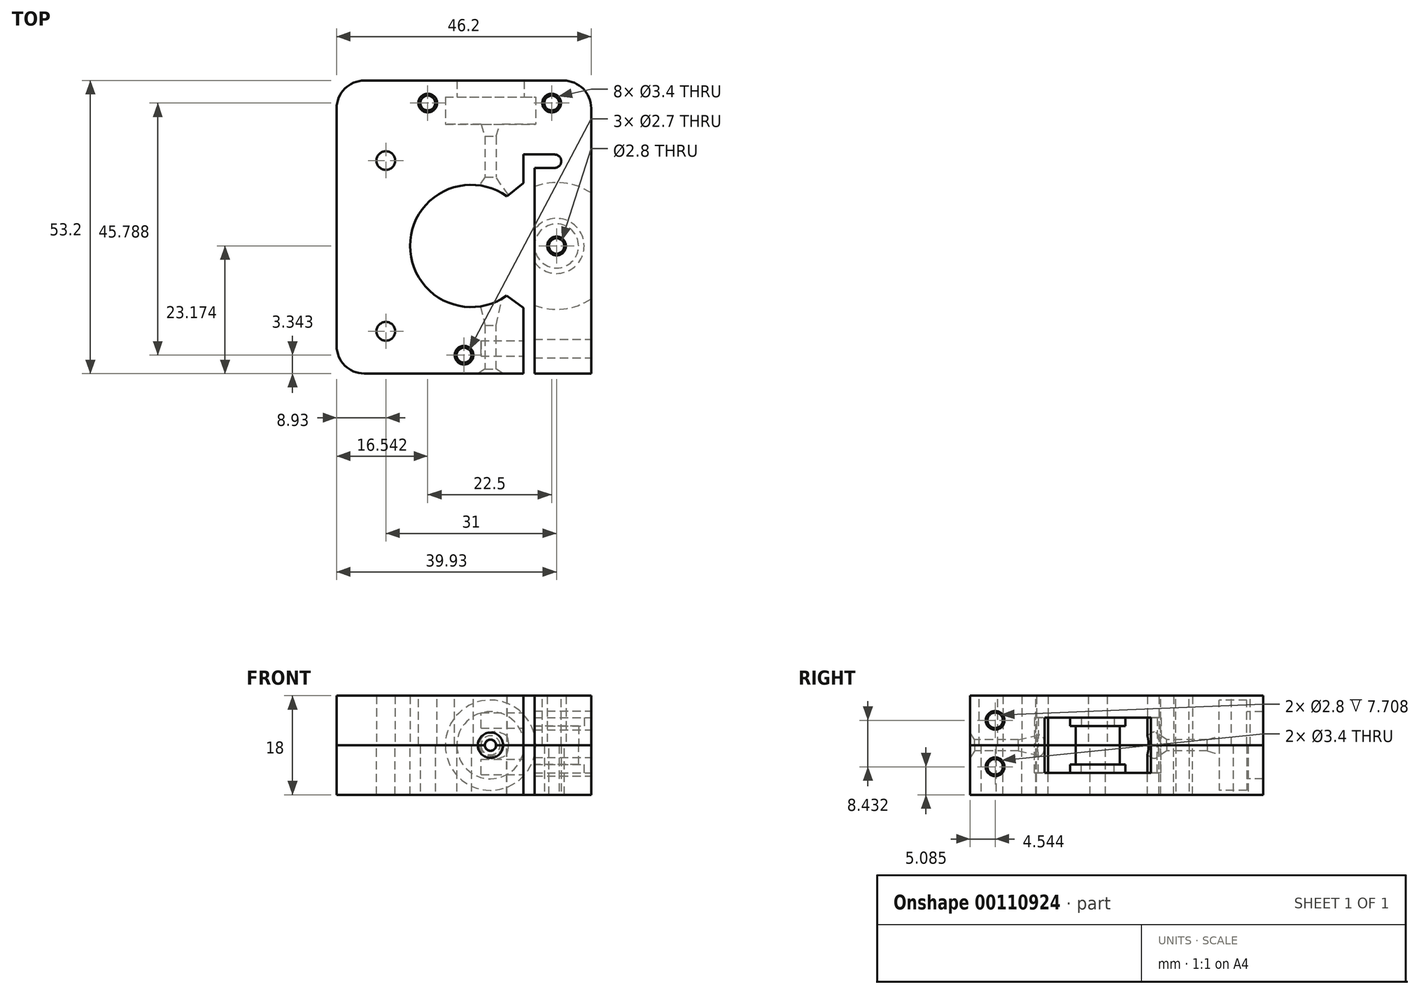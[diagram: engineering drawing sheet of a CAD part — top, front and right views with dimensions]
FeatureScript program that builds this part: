
annotation { "Feature Type Name" : "Feature", "Feature Type Description" : "" }
export const myFeature = defineFeature(function(context is Context, id is Id, definition is map)
    precondition{}
    {
        {
            var Q0;
            Q0=qCreatedBy(makeId("Top.planeOp"),FACE);
            var sketch = newSketch(context, id + "F0", { "sketchPlane" : qUnion([Q0])});
            skLineSegment(sketch, "E0", {"start": v(-24.43, 35.85) * mm, "end": v(-24.43, -17.36) * mm});
            skLineSegment(sketch, "E1", {"start": v(-24.43, -17.36) * mm, "end": v(-24.43, -17.36) * mm});
            skLineSegment(sketch, "E2", {"start": v(-24.43, -17.36) * mm, "end": v(-24.43, -17.35) * mm});
            skLineSegment(sketch, "E3", {"start": v(-24.43, -17.35) * mm, "end": v(9.48, -17.35) * mm});
            skLineSegment(sketch, "E4", {"start": v(9.48, -17.35) * mm, "end": v(9.48, 22.43) * mm});
            skLineSegment(sketch, "E5", {"start": v(9.48, 22.43) * mm, "end": v(15.14, 22.43) * mm});
            skLineSegment(sketch, "E6", {"start": v(15.14, 20) * mm, "end": v(11.48, 20) * mm});
            skLineSegment(sketch, "E7", {"start": v(11.48, 20) * mm, "end": v(11.48, -17.35) * mm});
            skLineSegment(sketch, "E8", {"start": v(11.48, -17.35) * mm, "end": v(21.77, -17.35) * mm});
            skLineSegment(sketch, "E9", {"start": v(21.77, -17.35) * mm, "end": v(21.77, 35.85) * mm});
            skLineSegment(sketch, "E10", {"start": v(21.77, 35.85) * mm, "end": v(-24.43, 35.85) * mm});
            skCircle(sketch, "E11", {"center": v(-7.89, 31.78) * mm, "radius": 1.35 * mm});
            skCircle(sketch, "E12", {"center": v(14.61, 31.78) * mm, "radius": 1.35 * mm});
            skCircle(sketch, "E13", {"center": v(-1.3, -14) * mm, "radius": 1.35 * mm});
            skArc(sketch, "E14", {"start": v(15.14, 20) * mm, "mid": v(16.35, 21.21) * mm, "end": v(15.14, 22.43) * mm});
            skCircle(sketch, "E15", {"center": v(-7.89, 31.78) * mm, "radius": 1.7 * mm});
            skCircle(sketch, "E16", {"center": v(14.61, 31.78) * mm, "radius": 1.7 * mm});
            skCircle(sketch, "E17", {"center": v(-1.3, -14) * mm, "radius": 1.7 * mm});
            skSolve(sketch);
        }
        {
            var Q0;
            Q0=makeQuery(id+"F0.imprint","IMPRINT",FACE,{"disambiguationData":[TD([[makeQuery(id+"F0.imprint","IMPRINT",EDGE,{"derivedFrom":sQuery(id+"F0.wireOp",EDGE,"E0")}),1.0]])]});
            var Q1;
            Q1=makeQuery(id+"F0.imprint","IMPRINT",FACE,{"disambiguationData":[TD([[makeQuery(id+"F0.imprint","IMPRINT",EDGE,{"derivedFrom":sQuery(id+"F0.wireOp",EDGE,"E11")}),-1.0]])]});
            var Q2;
            Q2=makeQuery(id+"F0.imprint","IMPRINT",FACE,{"disambiguationData":[TD([[makeQuery(id+"F0.imprint","IMPRINT",EDGE,{"derivedFrom":sQuery(id+"F0.wireOp",EDGE,"E12")}),-1.0]])]});
            var Q3;
            Q3=makeQuery(id+"F0.imprint","IMPRINT",FACE,{"disambiguationData":[TD([[makeQuery(id+"F0.imprint","IMPRINT",EDGE,{"derivedFrom":sQuery(id+"F0.wireOp",EDGE,"E13")}),-1.0]])]});
            extrude(context, id + "F1", {"entities" : qUnion([Q0, Q1, Q2, Q3]), "depth" : 9 * mm});
        }
        {
            var Q0;
            Q0=makeQuery(id+"F1.opExtrude","CAP_FACE",FACE,{"disambiguationData":[OSD([sQuery(id+"F0.wireOp",EDGE,"E0"),sQuery(id+"F0.wireOp",EDGE,"E1"),sQuery(id+"F0.wireOp",EDGE,"E2"),sQuery(id+"F0.wireOp",EDGE,"E3"),sQuery(id+"F0.wireOp",EDGE,"E4"),sQuery(id+"F0.wireOp",EDGE,"E5"),sQuery(id+"F0.wireOp",EDGE,"E6"),sQuery(id+"F0.wireOp",EDGE,"E7"),sQuery(id+"F0.wireOp",EDGE,"E8"),sQuery(id+"F0.wireOp",EDGE,"E9"),sQuery(id+"F0.wireOp",EDGE,"E10"),sQuery(id+"F0.wireOp",EDGE,"604cad85-587a-4b7d-8070-06f4cba85480"),sQuery(id+"F0.wireOp",EDGE,"6e5e38c1-5bff-4efe-a8c5-b84022f0a049"),sQuery(id+"F0.wireOp",EDGE,"b8144507-9dd7-4af4-87a3-7b649dd00ae6"),sQuery(id+"F0.wireOp",EDGE,"b9c2cb7c-5e58-4995-888e-a78f0403fbb5"),sQuery(id+"F0.wireOp",EDGE,"885990ab-7576-4c23-8475-595d2769e284"),sQuery(id+"F0.wireOp",EDGE,"E11"),sQuery(id+"F0.wireOp",EDGE,"E12"),sQuery(id+"F0.wireOp",EDGE,"E13"),sQuery(id+"F0.wireOp",EDGE,"E14")])],"isStart":false});
            var sketch = newSketch(context, id + "F2", { "sketchPlane" : qUnion([Q0])});
            skCircle(sketch, "E18", {"center": v(0, 5.82) * mm, "radius": 11.1 * mm});
            skCircle(sketch, "E19", {"center": v(-15.5, 21.32) * mm, "radius": 1.7 * mm});
            skCircle(sketch, "E20", {"center": v(-15.5, -9.68) * mm, "radius": 1.7 * mm});
            skLineSegment(sketch, "E21", {"start": v(6.47, 14.84) * mm, "end": v(10.02, 17.67) * mm});
            skLineSegment(sketch, "E22", {"start": v(10.02, 17.67) * mm, "end": v(10.29, 10) * mm});
            skLineSegment(sketch, "E23", {"start": v(6.43, -3.22) * mm, "end": v(10.18, -5.93) * mm});
            skLineSegment(sketch, "E24", {"start": v(10.18, -5.93) * mm, "end": v(10.18, 1.4) * mm});
            skSolve(sketch);
        }
        {
            var Q0;
            Q0=qSketchRegion(id+"F2",true);
            extrude(context, id + "F3", {"entities" : qUnion([Q0]), "operationType" : NewBodyOperationType.REMOVE, "endBound" : BoundingType.THROUGH_ALL, "oppositeDirection" : true, "depth" : 25 * mm});
        }
        {
            var Q0;
            Q0=makeQuery(id+"F1.opExtrude","CAP_FACE",FACE,{"disambiguationData":[OSD([sQuery(id+"F0.wireOp",EDGE,"E0"),sQuery(id+"F0.wireOp",EDGE,"E1"),sQuery(id+"F0.wireOp",EDGE,"E2"),sQuery(id+"F0.wireOp",EDGE,"E3"),sQuery(id+"F0.wireOp",EDGE,"E4"),sQuery(id+"F0.wireOp",EDGE,"E5"),sQuery(id+"F0.wireOp",EDGE,"E6"),sQuery(id+"F0.wireOp",EDGE,"E7"),sQuery(id+"F0.wireOp",EDGE,"E8"),sQuery(id+"F0.wireOp",EDGE,"E9"),sQuery(id+"F0.wireOp",EDGE,"E10"),sQuery(id+"F0.wireOp",EDGE,"604cad85-587a-4b7d-8070-06f4cba85480"),sQuery(id+"F0.wireOp",EDGE,"6e5e38c1-5bff-4efe-a8c5-b84022f0a049"),sQuery(id+"F0.wireOp",EDGE,"E11"),sQuery(id+"F0.wireOp",EDGE,"E12"),sQuery(id+"F0.wireOp",EDGE,"E13"),sQuery(id+"F0.wireOp",EDGE,"E14")])],"isStart":false});
            var sketch = newSketch(context, id + "F4", { "sketchPlane" : qUnion([Q0])});
            skCircle(sketch, "E25", {"center": v(15.5, 5.82) * mm, "radius": 11.5 * mm});
            skCircle(sketch, "E26", {"center": v(15.5, 5.82) * mm, "radius": 5 * mm});
            skCircle(sketch, "E27", {"center": v(15.5, 5.82) * mm, "radius": 4 * mm});
            skLineSegment(sketch, "E28", {"start": v(0, 5.82) * mm, "end": v(31, 5.82) * mm, "construction": true});
            skCircle(sketch, "E29", {"center": v(15.5, 5.82) * mm, "radius": 1.4 * mm});
            skCircle(sketch, "E30", {"center": v(15.5, 5.82) * mm, "radius": 1.7 * mm});
            skSolve(sketch);
        }
        {
            var Q0;
            {var subQ0=sQuery(id+"F4.wireOp",EDGE,"E25");var subQ4=makeQuery(id+"F1.opExtrude","CAP_EDGE",EDGE,{"disambiguationData":[OSD([sQuery(id+"F0.wireOp",EDGE,"E7")])],"isStart":false});var subQ9=makeQuery(id+"F4.imprint","INTERSECT",VERTEX,{"disambiguationData":[OD(0.0)],"derivedFrom":[subQ4,subQ0]});Q0=makeQuery(id+"F4.imprint","IMPRINT",FACE,{"disambiguationData":[TD([[makeQuery(id+"F4.imprint","IMPRINT",EDGE,{"disambiguationData":[TD([[subQ9,1.0]])],"derivedFrom":subQ0}),1.0]])]});}
            extrude(context, id + "F5", {"entities" : qUnion([Q0]), "operationType" : NewBodyOperationType.REMOVE, "oppositeDirection" : true, "depth" : 5 * mm});
        }
        {
            var Q0;
            Q0=makeQuery(id+"F4.imprint","IMPRINT",FACE,{"disambiguationData":[TD([[makeQuery(id+"F4.imprint","IMPRINT",EDGE,{"derivedFrom":sQuery(id+"F4.wireOp",EDGE,"E27")}),-1.0]])]});
            extrude(context, id + "F6", {"entities" : qUnion([Q0]), "operationType" : NewBodyOperationType.REMOVE, "oppositeDirection" : true, "depth" : 3.5 * mm});
        }
        {
            var Q0;
            {var subQ0=sQuery(id+"F0.wireOp",EDGE,"E0");var subQ1=sQuery(id+"F0.wireOp",EDGE,"E1");var subQ2=sQuery(id+"F0.wireOp",EDGE,"E2");var subQ3=sQuery(id+"F0.wireOp",EDGE,"E3");var subQ4=sQuery(id+"F0.wireOp",EDGE,"E4");var subQ5=sQuery(id+"F0.wireOp",EDGE,"E5");var subQ6=sQuery(id+"F0.wireOp",EDGE,"E6");var subQ7=sQuery(id+"F0.wireOp",EDGE,"E7");var subQ8=sQuery(id+"F0.wireOp",EDGE,"E9");var subQ9=sQuery(id+"F0.wireOp",EDGE,"E10");var subQ10=sQuery(id+"F0.wireOp",EDGE,"604cad85-587a-4b7d-8070-06f4cba85480");var subQ11=sQuery(id+"F0.wireOp",EDGE,"6e5e38c1-5bff-4efe-a8c5-b84022f0a049");var subQ12=sQuery(id+"F0.wireOp",EDGE,"E11");var subQ13=sQuery(id+"F0.wireOp",EDGE,"E12");var subQ14=sQuery(id+"F0.wireOp",EDGE,"E13");var subQ15=sQuery(id+"F0.wireOp",EDGE,"E14");Q0=makeQuery(id+"F5.boolean.opBoolean","SPLIT",FACE,{"disambiguationData":[TD([makeQuery(id+"F1.opExtrude","SWEPT_FACE",FACE,{"disambiguationData":[OSD([subQ0])]})])],"derivedFrom":makeQuery(id+"F1.opExtrude","CAP_FACE",FACE,{"disambiguationData":[OSD([subQ0,subQ1,subQ2,subQ3,subQ4,subQ5,subQ6,subQ7,sQuery(id+"F0.wireOp",EDGE,"E8"),subQ8,subQ9,subQ10,subQ11,subQ12,subQ13,subQ14,subQ15])],"isStart":false})});}
            var sketch = newSketch(context, id + "F7", { "sketchPlane" : qUnion([Q0])});
            skLineSegment(sketch, "E31", {"start": v(3.5, 14.7) * mm, "end": v(3.5, 37.09) * mm});
            skLineSegment(sketch, "E32", {"start": v(0, 5.82) * mm, "end": v(31.4, 5.82) * mm, "construction": true});
            skLineSegment(sketch, "E33.0.MirrorCS", {"start": v(1.07, -17.43) * mm, "end": v(2.47, -16.55) * mm});
            skLineSegment(sketch, "E33.1.MirrorCS", {"start": v(3.5, -3.06) * mm, "end": v(3.5, -25.44) * mm});
            skLineSegment(sketch, "E33.2.MirrorCS", {"start": v(0.98, -25.44) * mm, "end": v(1.07, -17.43) * mm});
            skLineSegment(sketch, "E33.3.MirrorCS", {"start": v(1.31, -3.53) * mm, "end": v(3.5, -3.06) * mm});
            skLineSegment(sketch, "E33.4.MirrorCS", {"start": v(2.5, -8.56) * mm, "end": v(1.31, -3.53) * mm});
            skLineSegment(sketch, "E33.5.MirrorCS", {"start": v(2.47, -16.55) * mm, "end": v(2.5, -8.56) * mm});
            skLineSegment(sketch, "E33.6.MirrorCS", {"start": v(3.5, -25.44) * mm, "end": v(0.98, -25.44) * mm});
            skLineSegment(sketch, "E34", {"start": v(-2.6, 37.09) * mm, "end": v(-2.6, 32.89) * mm});
            skLineSegment(sketch, "E35", {"start": v(-2.6, 32.89) * mm, "end": v(-4.7, 32.89) * mm});
            skLineSegment(sketch, "E36", {"start": v(-4.7, 32.89) * mm, "end": v(-4.7, 27.89) * mm});
            skLineSegment(sketch, "E37", {"start": v(-4.7, 27.89) * mm, "end": v(1.77, 27.89) * mm});
            skLineSegment(sketch, "E38", {"start": v(1.77, 27.89) * mm, "end": v(2.5, 25.73) * mm});
            skLineSegment(sketch, "E39", {"start": v(2.5, 25.73) * mm, "end": v(2.5, 18.34) * mm});
            skLineSegment(sketch, "E40", {"start": v(-2.6, 37.09) * mm, "end": v(3.5, 37.09) * mm});
            skLineSegment(sketch, "E41", {"start": v(2.5, 18.34) * mm, "end": v(0, 14.7) * mm});
            skLineSegment(sketch, "E42", {"start": v(0, 14.7) * mm, "end": v(3.5, 14.7) * mm});
            skSolve(sketch);
        }
        {
            var Q0;
            Q0=qSketchRegion(id+"F7",true);
            var Q1;
            Q1=sQuery(id+"F7.wireOp",EDGE,"E31");
            revolve(context, id + "F8", {"entities" : qUnion([Q0]), "axis" : qUnion([Q1]), "revolveType" : RevolveType.FULL});
        }
        {
            var Q0;
            Q0=makeQuery(id+"F8.opRevolve","SWEPT_BODY",BODY,{"disambiguationData":[OSD([sQuery(id+"F7.wireOp",EDGE,"0e4a01cc-4869-4b9d-8ca2-1c94110d196d"),sQuery(id+"F7.wireOp",EDGE,"4d913e13-2244-4a79-84d2-82f6c5de00b3"),sQuery(id+"F7.wireOp",EDGE,"1203443b-fa58-4cec-9fe4-144960d3b7c2"),sQuery(id+"F7.wireOp",EDGE,"f73e5a92-9274-40af-91db-ab5fa52ec61f"),sQuery(id+"F7.wireOp",EDGE,"4cc6588a-36a6-4115-9f4e-735cf5f17870"),sQuery(id+"F7.wireOp",EDGE,"E31"),sQuery(id+"F7.wireOp",EDGE,"0bbee7b9-97e0-41c3-ac0e-625151f8027d")])]});
            var Q1;
            Q1=makeQuery(id+"F1.opExtrude","SWEPT_BODY",BODY,{"disambiguationData":[OSD([sQuery(id+"F0.wireOp",EDGE,"E0"),sQuery(id+"F0.wireOp",EDGE,"E1"),sQuery(id+"F0.wireOp",EDGE,"E2"),sQuery(id+"F0.wireOp",EDGE,"E3"),sQuery(id+"F0.wireOp",EDGE,"E4"),sQuery(id+"F0.wireOp",EDGE,"E5"),sQuery(id+"F0.wireOp",EDGE,"E6"),sQuery(id+"F0.wireOp",EDGE,"E7"),sQuery(id+"F0.wireOp",EDGE,"E8"),sQuery(id+"F0.wireOp",EDGE,"E9"),sQuery(id+"F0.wireOp",EDGE,"E10"),sQuery(id+"F0.wireOp",EDGE,"604cad85-587a-4b7d-8070-06f4cba85480"),sQuery(id+"F0.wireOp",EDGE,"6e5e38c1-5bff-4efe-a8c5-b84022f0a049"),sQuery(id+"F0.wireOp",EDGE,"E11"),sQuery(id+"F0.wireOp",EDGE,"E12"),sQuery(id+"F0.wireOp",EDGE,"E13"),sQuery(id+"F0.wireOp",EDGE,"E14")])]});
            booleanBodies(context, id + "F9", {"operationType" : BooleanOperationType.SUBTRACTION, "tools" : qUnion([Q0]), "targets" : qUnion([Q1]), "keepTools" : true});
        }
        {
            var Q0;
            Q0=makeQuery(id+"F8.opRevolve","SWEPT_BODY",BODY,{"disambiguationData":[OSD([sQuery(id+"F7.wireOp",EDGE,"E33.0.MirrorCS"),sQuery(id+"F7.wireOp",EDGE,"E33.1.MirrorCS"),sQuery(id+"F7.wireOp",EDGE,"E33.2.MirrorCS"),sQuery(id+"F7.wireOp",EDGE,"E33.3.MirrorCS"),sQuery(id+"F7.wireOp",EDGE,"E33.4.MirrorCS"),sQuery(id+"F7.wireOp",EDGE,"E33.5.MirrorCS"),sQuery(id+"F7.wireOp",EDGE,"E33.6.MirrorCS")])]});
            var Q1;
            Q1=makeQuery(id+"F1.opExtrude","SWEPT_BODY",BODY,{"disambiguationData":[OSD([sQuery(id+"F0.wireOp",EDGE,"E0"),sQuery(id+"F0.wireOp",EDGE,"E1"),sQuery(id+"F0.wireOp",EDGE,"E2"),sQuery(id+"F0.wireOp",EDGE,"E3"),sQuery(id+"F0.wireOp",EDGE,"E4"),sQuery(id+"F0.wireOp",EDGE,"E5"),sQuery(id+"F0.wireOp",EDGE,"E6"),sQuery(id+"F0.wireOp",EDGE,"E7"),sQuery(id+"F0.wireOp",EDGE,"E8"),sQuery(id+"F0.wireOp",EDGE,"E9"),sQuery(id+"F0.wireOp",EDGE,"E10"),sQuery(id+"F0.wireOp",EDGE,"604cad85-587a-4b7d-8070-06f4cba85480"),sQuery(id+"F0.wireOp",EDGE,"6e5e38c1-5bff-4efe-a8c5-b84022f0a049"),sQuery(id+"F0.wireOp",EDGE,"E11"),sQuery(id+"F0.wireOp",EDGE,"E12"),sQuery(id+"F0.wireOp",EDGE,"E13"),sQuery(id+"F0.wireOp",EDGE,"E14")])]});
            booleanBodies(context, id + "F10", {"operationType" : BooleanOperationType.SUBTRACTION, "tools" : qUnion([Q0]), "targets" : qUnion([Q1]), "keepTools" : true});
        }
        {
            var Q0;
            Q0=qSketchRegion(id+"F0",true);
            extrude(context, id + "F11", {"entities" : qUnion([Q0]), "oppositeDirection" : true, "depth" : 9 * mm});
        }
        {
            var Q0;
            Q0=makeQuery(id+"F11.opExtrude","SWEPT_BODY",BODY,{"disambiguationData":[OSD([sQuery(id+"F0.wireOp",EDGE,"E0"),sQuery(id+"F0.wireOp",EDGE,"E3"),sQuery(id+"F0.wireOp",EDGE,"E4"),sQuery(id+"F0.wireOp",EDGE,"E5"),sQuery(id+"F0.wireOp",EDGE,"E6"),sQuery(id+"F0.wireOp",EDGE,"E7"),sQuery(id+"F0.wireOp",EDGE,"E8"),sQuery(id+"F0.wireOp",EDGE,"E9"),sQuery(id+"F0.wireOp",EDGE,"E10"),sQuery(id+"F0.wireOp",EDGE,"E11"),sQuery(id+"F0.wireOp",EDGE,"E12"),sQuery(id+"F0.wireOp",EDGE,"E13"),sQuery(id+"F0.wireOp",EDGE,"E14")])]});
            transform(context, id + "F12", {"entities" : qUnion([Q0]), "transformType" : TransformType.TRANSLATION_3D, "dx" : 0 * mm, "dy" : 0 * mm, "dz" : 18 * mm, "makeCopy" : false});
        }
        {
            var Q0;
            Q0=qSketchRegion(id+"F2",true);
            extrude(context, id + "F13", {"entities" : qUnion([Q0]), "operationType" : NewBodyOperationType.REMOVE, "endBound" : BoundingType.THROUGH_ALL, "depth" : 25 * mm});
        }
        {
            var Q0;
            {var subQ3=sQuery(id+"F4.wireOp",EDGE,"E25");var subQ7=makeQuery(id+"F1.opExtrude","CAP_EDGE",EDGE,{"disambiguationData":[OSD([sQuery(id+"F0.wireOp",EDGE,"E9")])],"isStart":false});var subQ9=makeQuery(id+"F4.imprint","INTERSECT",VERTEX,{"disambiguationData":[OD(0.0)],"derivedFrom":[subQ7,subQ3]});Q0=makeQuery(id+"F4.imprint","IMPRINT",FACE,{"disambiguationData":[TD([[makeQuery(id+"F4.imprint","IMPRINT",EDGE,{"disambiguationData":[TD([[subQ9,-1.0]])],"derivedFrom":subQ3}),1.0]])]});}
            extrude(context, id + "F14", {"entities" : qUnion([Q0]), "operationType" : NewBodyOperationType.REMOVE, "depth" : 5 * mm});
        }
        {
            var Q0;
            Q0=makeQuery(id+"F4.imprint","IMPRINT",FACE,{"disambiguationData":[TD([[makeQuery(id+"F4.imprint","IMPRINT",EDGE,{"derivedFrom":sQuery(id+"F4.wireOp",EDGE,"E27")}),-1.0]])]});
            extrude(context, id + "F15", {"entities" : qUnion([Q0]), "operationType" : NewBodyOperationType.REMOVE, "depth" : 3.5 * mm});
        }
        {
            var Q0;
            Q0=makeQuery(id+"F8.opRevolve","SWEPT_BODY",BODY,{"disambiguationData":[OSD([sQuery(id+"F7.wireOp",EDGE,"0e4a01cc-4869-4b9d-8ca2-1c94110d196d"),sQuery(id+"F7.wireOp",EDGE,"4d913e13-2244-4a79-84d2-82f6c5de00b3"),sQuery(id+"F7.wireOp",EDGE,"1203443b-fa58-4cec-9fe4-144960d3b7c2"),sQuery(id+"F7.wireOp",EDGE,"f73e5a92-9274-40af-91db-ab5fa52ec61f"),sQuery(id+"F7.wireOp",EDGE,"4cc6588a-36a6-4115-9f4e-735cf5f17870"),sQuery(id+"F7.wireOp",EDGE,"E31"),sQuery(id+"F7.wireOp",EDGE,"0bbee7b9-97e0-41c3-ac0e-625151f8027d")])]});
            var Q1;
            Q1=makeQuery(id+"F11.opExtrude","SWEPT_BODY",BODY,{"disambiguationData":[OSD([sQuery(id+"F0.wireOp",EDGE,"E0"),sQuery(id+"F0.wireOp",EDGE,"E3"),sQuery(id+"F0.wireOp",EDGE,"E4"),sQuery(id+"F0.wireOp",EDGE,"E5"),sQuery(id+"F0.wireOp",EDGE,"E6"),sQuery(id+"F0.wireOp",EDGE,"E7"),sQuery(id+"F0.wireOp",EDGE,"E8"),sQuery(id+"F0.wireOp",EDGE,"E9"),sQuery(id+"F0.wireOp",EDGE,"E10"),sQuery(id+"F0.wireOp",EDGE,"E11"),sQuery(id+"F0.wireOp",EDGE,"E12"),sQuery(id+"F0.wireOp",EDGE,"E13"),sQuery(id+"F0.wireOp",EDGE,"E14")])]});
            booleanBodies(context, id + "F16", {"operationType" : BooleanOperationType.SUBTRACTION, "tools" : qUnion([Q0]), "targets" : qUnion([Q1])});
        }
        {
            var Q0;
            Q0=makeQuery(id+"F8.opRevolve","SWEPT_BODY",BODY,{"disambiguationData":[OSD([sQuery(id+"F7.wireOp",EDGE,"E33.0.MirrorCS"),sQuery(id+"F7.wireOp",EDGE,"E33.1.MirrorCS"),sQuery(id+"F7.wireOp",EDGE,"E33.2.MirrorCS"),sQuery(id+"F7.wireOp",EDGE,"E33.3.MirrorCS"),sQuery(id+"F7.wireOp",EDGE,"E33.4.MirrorCS"),sQuery(id+"F7.wireOp",EDGE,"E33.5.MirrorCS"),sQuery(id+"F7.wireOp",EDGE,"E33.6.MirrorCS")])]});
            var Q1;
            Q1=makeQuery(id+"F11.opExtrude","SWEPT_BODY",BODY,{"disambiguationData":[OSD([sQuery(id+"F0.wireOp",EDGE,"E0"),sQuery(id+"F0.wireOp",EDGE,"E3"),sQuery(id+"F0.wireOp",EDGE,"E4"),sQuery(id+"F0.wireOp",EDGE,"E5"),sQuery(id+"F0.wireOp",EDGE,"E6"),sQuery(id+"F0.wireOp",EDGE,"E7"),sQuery(id+"F0.wireOp",EDGE,"E8"),sQuery(id+"F0.wireOp",EDGE,"E9"),sQuery(id+"F0.wireOp",EDGE,"E10"),sQuery(id+"F0.wireOp",EDGE,"E11"),sQuery(id+"F0.wireOp",EDGE,"E12"),sQuery(id+"F0.wireOp",EDGE,"E13"),sQuery(id+"F0.wireOp",EDGE,"E14")])]});
            booleanBodies(context, id + "F17", {"operationType" : BooleanOperationType.SUBTRACTION, "tools" : qUnion([Q0]), "targets" : qUnion([Q1])});
        }
        {
            var Q0;
            Q0=makeQuery(id+"F11.opExtrude","SWEPT_FACE",FACE,{"disambiguationData":[OSD([sQuery(id+"F0.wireOp",EDGE,"E9")])]});
            var sketch = newSketch(context, id + "F18", { "sketchPlane" : qUnion([Q0])});
            skCircle(sketch, "E43", {"center": v(-12.8, 13.52) * mm, "radius": 1.7 * mm});
            skCircle(sketch, "E44", {"center": v(-12.8, 13.52) * mm, "radius": 1.4 * mm});
            skCircle(sketch, "E45", {"center": v(-12.8, 5.09) * mm, "radius": 1.7 * mm});
            skCircle(sketch, "E46", {"center": v(-12.8, 5.09) * mm, "radius": 1.4 * mm});
            skSolve(sketch);
        }
        {
            var Q0;
            Q0=makeQuery(id+"F18.imprint","IMPRINT",FACE,{"disambiguationData":[TD([[makeQuery(id+"F18.imprint","IMPRINT",EDGE,{"derivedFrom":sQuery(id+"F18.wireOp",EDGE,"E44")}),1.0]])]});
            extrude(context, id + "F19", {"entities" : qUnion([Q0]), "operationType" : NewBodyOperationType.REMOVE, "oppositeDirection" : true, "depth" : 20 * mm});
        }
        {
            var Q0;
            Q0=makeQuery(id+"F18.imprint","IMPRINT",FACE,{"disambiguationData":[TD([[makeQuery(id+"F18.imprint","IMPRINT",EDGE,{"derivedFrom":sQuery(id+"F18.wireOp",EDGE,"E43")}),1.0]])]});
            extrude(context, id + "F20", {"entities" : qUnion([Q0]), "operationType" : NewBodyOperationType.REMOVE, "oppositeDirection" : true, "depth" : 11 * mm});
        }
        {
            var Q0;
            Q0=makeQuery(id+"F18.imprint","IMPRINT",FACE,{"disambiguationData":[TD([[makeQuery(id+"F18.imprint","IMPRINT",EDGE,{"derivedFrom":sQuery(id+"F18.wireOp",EDGE,"E46")}),1.0]])]});
            extrude(context, id + "F21", {"entities" : qUnion([Q0]), "operationType" : NewBodyOperationType.REMOVE, "oppositeDirection" : true, "depth" : 20 * mm});
        }
        {
            var Q0;
            Q0=makeQuery(id+"F18.imprint","IMPRINT",FACE,{"disambiguationData":[TD([[makeQuery(id+"F18.imprint","IMPRINT",EDGE,{"derivedFrom":sQuery(id+"F18.wireOp",EDGE,"E45")}),1.0]])]});
            extrude(context, id + "F22", {"entities" : qUnion([Q0]), "operationType" : NewBodyOperationType.REMOVE, "oppositeDirection" : true, "depth" : 11 * mm});
        }
        {
            var Q0;
            Q0=makeQuery(id+"F4.imprint","IMPRINT",FACE,{"disambiguationData":[TD([[makeQuery(id+"F4.imprint","IMPRINT",EDGE,{"derivedFrom":sQuery(id+"F4.wireOp",EDGE,"E29")}),1.0]])]});
            extrude(context, id + "F23", {"entities" : qUnion([Q0]), "operationType" : NewBodyOperationType.REMOVE, "endBound" : BoundingType.THROUGH_ALL, "oppositeDirection" : true, "depth" : 25 * mm});
        }
        {
            var Q0;
            Q0=makeQuery(id+"F4.imprint","IMPRINT",FACE,{"disambiguationData":[TD([[makeQuery(id+"F4.imprint","IMPRINT",EDGE,{"derivedFrom":sQuery(id+"F4.wireOp",EDGE,"E29")}),1.0]])]});
            var Q1;
            Q1=makeQuery(id+"F4.imprint","IMPRINT",FACE,{"disambiguationData":[TD([[makeQuery(id+"F4.imprint","IMPRINT",EDGE,{"derivedFrom":sQuery(id+"F4.wireOp",EDGE,"E29")}),-1.0]])]});
            extrude(context, id + "F24", {"entities" : qUnion([Q0, Q1]), "operationType" : NewBodyOperationType.REMOVE, "endBound" : BoundingType.THROUGH_ALL, "depth" : 25 * mm});
        }
        {
            var Q0;
            Q0=makeQuery(id+"F11.opExtrude","SWEPT_EDGE",EDGE,{"disambiguationData":[OSD([sQuery(id+"F0.wireOp",EDGE,"E9"),sQuery(id+"F0.wireOp",EDGE,"E10")])]});
            var Q1;
            Q1=makeQuery(id+"F1.opExtrude","SWEPT_EDGE",EDGE,{"disambiguationData":[OSD([sQuery(id+"F0.wireOp",EDGE,"E9"),sQuery(id+"F0.wireOp",EDGE,"E10")])]});
            var Q2;
            Q2=makeQuery(id+"F11.opExtrude","SWEPT_EDGE",EDGE,{"disambiguationData":[OSD([sQuery(id+"F0.wireOp",EDGE,"E0"),sQuery(id+"F0.wireOp",EDGE,"E10")])]});
            var Q3;
            Q3=makeQuery(id+"F1.opExtrude","SWEPT_EDGE",EDGE,{"disambiguationData":[OSD([sQuery(id+"F0.wireOp",EDGE,"E0"),sQuery(id+"F0.wireOp",EDGE,"E10")])]});
            var Q4;
            Q4=makeQuery(id+"F11.opExtrude","SWEPT_EDGE",EDGE,{"disambiguationData":[OSD([sQuery(id+"F0.wireOp",EDGE,"E0"),sQuery(id+"F0.wireOp",EDGE,"E3")])]});
            var Q5;
            Q5=makeQuery(id+"F1.opExtrude","SWEPT_EDGE",EDGE,{"disambiguationData":[OSD([sQuery(id+"F0.wireOp",EDGE,"E0"),sQuery(id+"F0.wireOp",EDGE,"E3")])]});
            fillet(context, id + "F25", {"entities" : qUnion([Q0, Q1, Q2, Q3, Q4, Q5]), "radius" : 5 * mm, "tangentPropagation" : true, "allowEdgeOverflow" : false});
        }
    });
